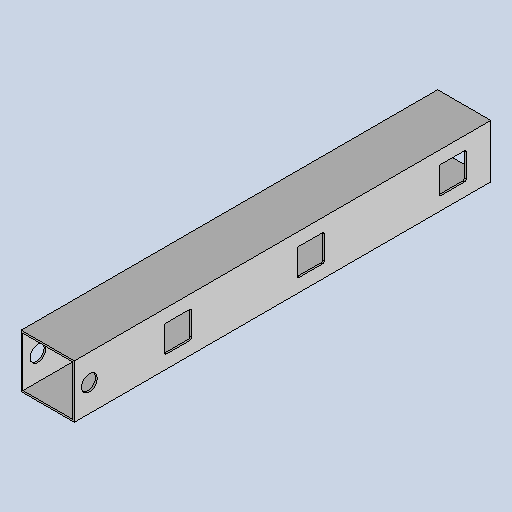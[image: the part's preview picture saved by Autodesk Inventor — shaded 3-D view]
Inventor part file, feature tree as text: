
AUTODESK INVENTOR PART (.ipt)
format: ipt  version: 2025.1 (Build 291241020, 241B)  size: 224,256 bytes
history: native  units: mm
features: sketch x4, projected_geometry x3, extrude x2, fillet x1
ambient origin geometry x8: Origin, YZ Plane, XZ Plane, XY Plane, X Axis, Y Axis, Z Axis, Center Point
bodies: Body1 (feature_tree)
feature tree (10):
  extrude  "Extrusion3"  Depth=60.0mm
  extrude  "Extrusion4"  Depth=2.0mm
  sketch  "Sketch11"  dims[d177=30.5mm]
  sketch  "Sketch13"  dims[d178=30.5mm d179=0.0mm d180=0.0mm d181=47.0mm d182=90.0mm d183=250.0mm d184=400.0mm d185=500.0mm d186=18.0mm d187=2.0mm]
  fillet  "Fillet1"  Radius=470.0mm
  sketch  "Sketch9"  dims[d61=500.0mm d172=60.0mm]
  sketch  "Sketch10"  dims[d173=60.0mm d174=2.0mm d175=470.0mm d176=0.0mm]
  projected_geometry  "Projected Loop3"
  projected_geometry  "Projected Loop4"
  projected_geometry  "Projected Loop5"
